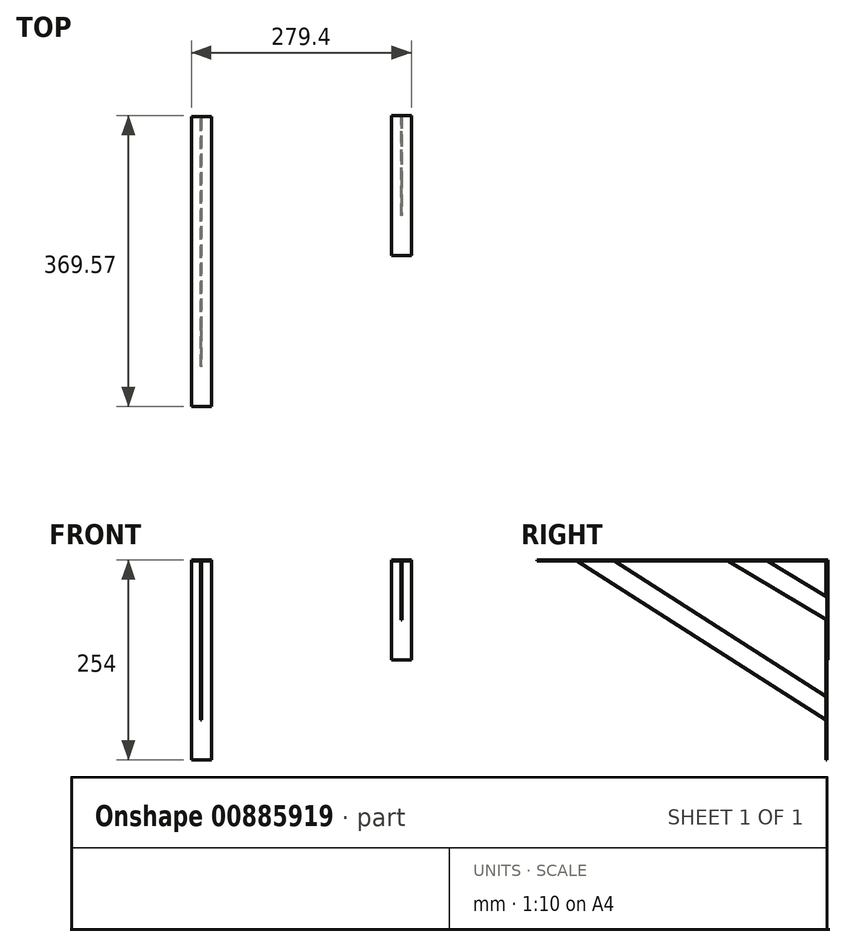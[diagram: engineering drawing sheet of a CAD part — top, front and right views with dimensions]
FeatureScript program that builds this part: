
annotation { "Feature Type Name" : "Feature", "Feature Type Description" : "" }
export const myFeature = defineFeature(function(context is Context, id is Id, definition is map)
    precondition{}
    {
        {
            var Q0;
            Q0=qCreatedBy(makeId("Right.planeOp"),FACE);
            var sketch = newSketch(context, id + "F0", { "sketchPlane" : qUnion([Q0])});
            skLineSegment(sketch, "E0", {"start": v(-368.3, 0) * mm, "end": v(0, 0) * mm});
            skLineSegment(sketch, "E1", {"start": v(0, 0) * mm, "end": v(0, -254) * mm});
            skLineSegment(sketch, "E2", {"start": v(-368.3, 0) * mm, "end": v(-368.3, -1.27) * mm});
            skLineSegment(sketch, "E3", {"start": v(-368.3, -1.27) * mm, "end": v(-1.27, -1.27) * mm});
            skLineSegment(sketch, "E4", {"start": v(-1.27, -1.27) * mm, "end": v(-1.27, -254) * mm});
            skLineSegment(sketch, "E5", {"start": v(-1.27, -254) * mm, "end": v(0, -254) * mm});
            skSolve(sketch);
        }
        {
            var Q0;
            Q0 = qSketchRegion(id + "F0", true);
            extrude(context, id + "F1", {"entities" : qUnion([Q0]), "endBound" : BoundingType.SYMMETRIC, "depth" : 25.4 * mm, "offsetDistance" : 25.4 * mm});
        }
        {
            var Q0;
            Q0=qCreatedBy(makeId("Right.planeOp"),FACE);
            var sketch = newSketch(context, id + "F2", { "sketchPlane" : qUnion([Q0])});
            skLineSegment(sketch, "E6", {"start": v(-270.3, -1.27) * mm, "end": v(-317.5, -1.27) * mm});
            skLineSegment(sketch, "E7", {"start": v(-317.5, -1.27) * mm, "end": v(-1.27, -203.2) * mm});
            skLineSegment(sketch, "E8", {"start": v(-1.27, -203.2) * mm, "end": v(-1.27, -173.06) * mm});
            skLineSegment(sketch, "E9", {"start": v(-1.27, -173.06) * mm, "end": v(-270.3, -1.27) * mm});
            skSolve(sketch);
        }
        {
            var Q0;
            Q0 = qSketchRegion(id + "F2", true);
            extrude(context, id + "F3", {"entities" : qUnion([Q0]), "operationType" : NewBodyOperationType.ADD, "endBound" : BoundingType.SYMMETRIC, "depth" : 1.27 * mm, "offsetDistance" : 25.4 * mm});
        }
        {
            var Q0;
            Q0=qCreatedBy(makeId("Right.planeOp"),FACE);
            cPlane(context, id + "F4", {"entities" : qUnion([Q0]), "cplaneType" : CPlaneType.OFFSET, "offset" : 254 * mm, "width" : 152.4 * mm, "height" : 152.4 * mm});
        }
        {
            var Q0;
            Q0=qCreatedBy(id+"F4.planeOp",FACE);
            var sketch = newSketch(context, id + "F5", { "sketchPlane" : qUnion([Q0])});
            skLineSegment(sketch, "E10", {"start": v(-176.53, 0) * mm, "end": v(1.27, 0) * mm});
            skLineSegment(sketch, "E11", {"start": v(1.27, 0) * mm, "end": v(1.27, -127) * mm});
            skLineSegment(sketch, "E12", {"start": v(-176.53, 0) * mm, "end": v(-176.53, -1.27) * mm});
            skLineSegment(sketch, "E13", {"start": v(-176.53, -1.27) * mm, "end": v(0, -1.27) * mm});
            skLineSegment(sketch, "E14", {"start": v(0, -1.27) * mm, "end": v(0, -127) * mm});
            skLineSegment(sketch, "E15", {"start": v(0, -127) * mm, "end": v(1.27, -127) * mm});
            skSolve(sketch);
        }
        {
            var Q0;
            Q0 = qSketchRegion(id + "F5", true);
            extrude(context, id + "F6", {"entities" : qUnion([Q0]), "endBound" : BoundingType.SYMMETRIC, "depth" : 25.4 * mm, "offsetDistance" : 25.4 * mm});
        }
        {
            var Q0;
            Q0=qCreatedBy(id+"F4.planeOp",FACE);
            var sketch = newSketch(context, id + "F7", { "sketchPlane" : qUnion([Q0])});
            skLineSegment(sketch, "E16", {"start": v(-76.11, -1.27) * mm, "end": v(-125.73, -1.27) * mm});
            skLineSegment(sketch, "E17", {"start": v(-125.73, -1.27) * mm, "end": v(0, -76.2) * mm});
            skLineSegment(sketch, "E18", {"start": v(0, -76.2) * mm, "end": v(0, -46.63) * mm});
            skLineSegment(sketch, "E19", {"start": v(0, -46.63) * mm, "end": v(-76.11, -1.27) * mm});
            skSolve(sketch);
        }
        {
            var Q0;
            Q0 = qSketchRegion(id + "F7", true);
            extrude(context, id + "F8", {"entities" : qUnion([Q0]), "operationType" : NewBodyOperationType.ADD, "endBound" : BoundingType.SYMMETRIC, "depth" : 1.27 * mm, "offsetDistance" : 25.4 * mm});
        }
    });
